# Revit family: Iso-VS
name_source: partatom
category: Mechanical Equipment
units: mm (PartAtom-declared; Revit-internal decimal feet)

## family parameters
Always vertical = Yes
Cut with Voids When Loaded = No
OmniClass Number = 23.75.00.00
OmniClass Title = Climate Control (HVAC)
Part Type = Normal
Room Calculation Point = No
Round Connector Dimension = Use Diameter
Shared = No
Work Plane-Based = No

## types (18) — shared parameters
00_20_Manufacturer = Blauberg
00_20_Name = Sound-insulated smoke extraction fan
Amperage = 0 A
Casing Material = galvanized steel
Casing Material Fan = Metal, painted, blue, matte RAL 5007
Filter = G4
Frequency = 50 Hz
Load Classification = HVAC
Maintenance zone material = <By Category>
Maximum Air Flow = 28500.0 m³/h
zero-valued in all types: Default Elevation

## per-type parameters (varying)
| type | A | A1 | B1 | D | Number of Fase | Power | Sound pressure level at 3 m distance | Voltage | Weight |
| Iso-VS 28-2D | 450 mm  [stored 1.47638 ft] | 190 mm  [stored 0.62336 ft] | 390 mm  [stored 1.27953 ft] | 280 mm  [stored 0.918635 ft] | 3 | 550 W | 0 dBA | 400 V | 39.00 kg |
| Iso-VS 28-2E | 450 mm  [stored 1.47638 ft] | 190 mm  [stored 0.62336 ft] | 390 mm  [stored 1.27953 ft] | 280 mm  [stored 0.918635 ft] | 1 | 550 W |  | 230 V | 39.00 kg |
| Iso-VS 31-2D | 500 mm  [stored 1.64042 ft] | 200 mm  [stored 0.656168 ft] | 440 mm  [stored 1.44357 ft] | 315 mm  [stored 1.03346 ft] | 1 | 1100 W |  | 400 V | 50.60 kg |
| Iso-VS 31-2E | 500 mm  [stored 1.64042 ft] | 200 mm  [stored 0.656168 ft] | 440 mm  [stored 1.44357 ft] | 315 mm  [stored 1.03346 ft] | 1 | 1100 W |  | 230 V | 50.60 kg |
| Iso-VS 31-4D | 500 mm  [stored 1.64042 ft] | 200 mm  [stored 0.656168 ft] | 440 mm  [stored 1.44357 ft] | 315 mm  [stored 1.03346 ft] | 1 | 250 W |  | 400 V | 46.50 kg |
| Iso-VS 31-4E | 500 mm  [stored 1.64042 ft] | 200 mm  [stored 0.656168 ft] | 440 mm  [stored 1.44357 ft] | 315 mm  [stored 1.03346 ft] | 1 | 250 W |  | 230 V | 46.50 kg |
| Iso-VS 35-4D | 600 mm | 225 mm  [stored 0.738189 ft] | 540 mm  [stored 1.77165 ft] | 355 mm | 1 | 370 W |  | 400 V | 61.60 kg |
| Iso-VS 35-4E | 600 mm | 225 mm  [stored 0.738189 ft] | 540 mm  [stored 1.77165 ft] | 355 mm | 1 | 370 W |  | 230 V | 61.60 kg |
| Iso-VS 40-4D | 670 mm  [stored 2.19816 ft] | 252 mm  [stored 0.826772 ft] | 610 mm  [stored 2.00131 ft] | 400 mm  [stored 1.31234 ft] | 1 | 550 W |  | 400 V | 72.00 kg |
| Iso-VS 40-4E | 670 mm  [stored 2.19816 ft] | 252 mm  [stored 0.826772 ft] | 610 mm  [stored 2.00131 ft] | 400 mm  [stored 1.31234 ft] | 1 | 550 W |  | 230 V | 65.70 kg |
| Iso-VS 45-4D | 700 mm  [stored 2.29659 ft] | 282 mm | 640 mm  [stored 2.09974 ft] | 450 mm  [stored 1.47638 ft] | 1 | 750 W |  | 230 V | 76.70 kg |
| Iso-VS 45-4E | 700 mm  [stored 2.29659 ft] | 282 mm | 640 mm  [stored 2.09974 ft] | 450 mm  [stored 1.47638 ft] | 1 | 750 W |  | 230 V | 76.70 kg |
| Iso-VS 50-4D | 820 mm  [stored 2.69029 ft] | 321 mm  [stored 1.05315 ft] | 760 mm | 500 mm  [stored 1.64042 ft] | 1 | 1500 W |  | 400 V | 111.00 kg |
| Iso-VS 56-4D | 900 mm  [stored 2.95276 ft] | 365 mm  [stored 1.19751 ft] | 840 mm  [stored 2.75591 ft] | 560 mm  [stored 1.83727 ft] | 1 | 3000 W |  | 400 V | 144.00 kg |
| Iso-VS 63-4D | 1000 mm  [stored 3.28084 ft] | 409 mm  [stored 1.34186 ft] | 940 mm  [stored 3.08399 ft] | 630 mm  [stored 2.06693 ft] | 1 | 4000 W |  | 400 V | 166.00 kg |
| Iso-VS 71-4D | 1075 mm | 456 mm  [stored 1.49606 ft] | 1015 mm  [stored 3.33005 ft] | 710 mm | 1 | 7500 W |  | 400 V | 262.00 kg |
| Iso-VS 71-6D | 1075 mm | 456 mm  [stored 1.49606 ft] | 1015 mm  [stored 3.33005 ft] | 710 mm | 1 | 2200 W |  | 400 V | 237.00 kg |
| Iso-VS 80-6D | 1175 mm | 506 mm  [stored 1.6601 ft] | 1115 mm  [stored 3.65814 ft] | 800 mm  [stored 2.62467 ft] | 1 | 4000 W |  | 400 V | 311.00 kg |

note: column(s) folded — value = type name in every type: 00_20_Type

note: [stored X ft] marks values corroborated as IEEE doubles in the binary element streams (Revit-internal decimal feet)

## geometry (parser evidence)
native form markers: Sweep x40
no freeform markers — native parametric forms only
